FCSTD DOCUMENT  (FreeCAD 1.0R38641 +468 (Git))
Label: Lower_Arm
License: All rights reserved
LicenseURL: https://en.wikipedia.org/wiki/All_rights_reserved
objects: App::Link×2, App::FeaturePython×1, Assembly::JointGroup×1, Assembly::AssemblyObject×1, App::Part×1, Mesh::Feature×1
EXTERNAL_REF file=F2.FCStd obj=F004
EXTERNAL_REF file=F1.FCStd obj=F003

FEATURE [App::Link] F004
  LinkedObject = -> <external F2.FCStd>#F004
FEATURE [App::FeaturePython] GroundedJoint  # Assembly grounded joint (typed FeaturePython)
  ObjectToGround = -> F004
FEATURE [Assembly::JointGroup] Joints
  Group = -> [GroundedJoint]
FEATURE [App::Link] F003
  LinkedObject = -> <external F1.FCStd>#F003
FEATURE [Assembly::AssemblyObject] Assembly
  Group = -> [Joints,F004,GroundedJoint,F003]
  Origin = -> Origin
  Placement = pos=(-0.2,0,0) rot=(0,0,1;0rad)
  Type = Assembly
FEATURE [App::Part] Part
  Group = -> [Assembly]
  Origin = -> Origin001
  Placement = pos=(4.33e-14,183,-100.1) rot=(0.57735,-0.57735,-0.57735;4.18879rad)
FEATURE [Mesh::Feature] Mesh  label="Assembly (Meshed)"

RESOLVED EXTERNAL PARTS (link-assembly join: the EXTERNAL_REF files above that resolve inside this repo's crawl, each included once):
---- part F1.FCStd = doc fcstd_cdde5d6d9684 ----
FCSTD DOCUMENT  (FreeCAD 1.0R38641 +468 (Git))
Label: F1
License: All rights reserved
LicenseURL: https://en.wikipedia.org/wiki/All_rights_reserved
objects: Part::Feature×1, Part::Refine×1
note: 2 computed .brp shape members not serialized (recipe doc carries the construction recipe); baked Part::Feature solids carry a one-line shape summary decoded from their .brp

FEATURE [Part::Feature] F002
  shape: bbox 117.7 x 70.5 x 32.5 mm, 4992 faces, 0 solids (baked)
FEATURE [Part::Refine] F003
  Source = -> F002
---- part F2.FCStd = doc fcstd_562fae4db0e5 ----
FCSTD DOCUMENT  (FreeCAD 1.0R38641 +468 (Git))
Label: F2
License: All rights reserved
LicenseURL: https://en.wikipedia.org/wiki/All_rights_reserved
objects: Part::Feature×1, Part::Refine×1
note: 2 computed .brp shape members not serialized (recipe doc carries the construction recipe); baked Part::Feature solids carry a one-line shape summary decoded from their .brp

FEATURE [Part::Feature] F003
  shape: bbox 117.7 x 70.5 x 27.5 mm, 6340 faces, 0 solids (baked)
FEATURE [Part::Refine] F004
  Source = -> F003
